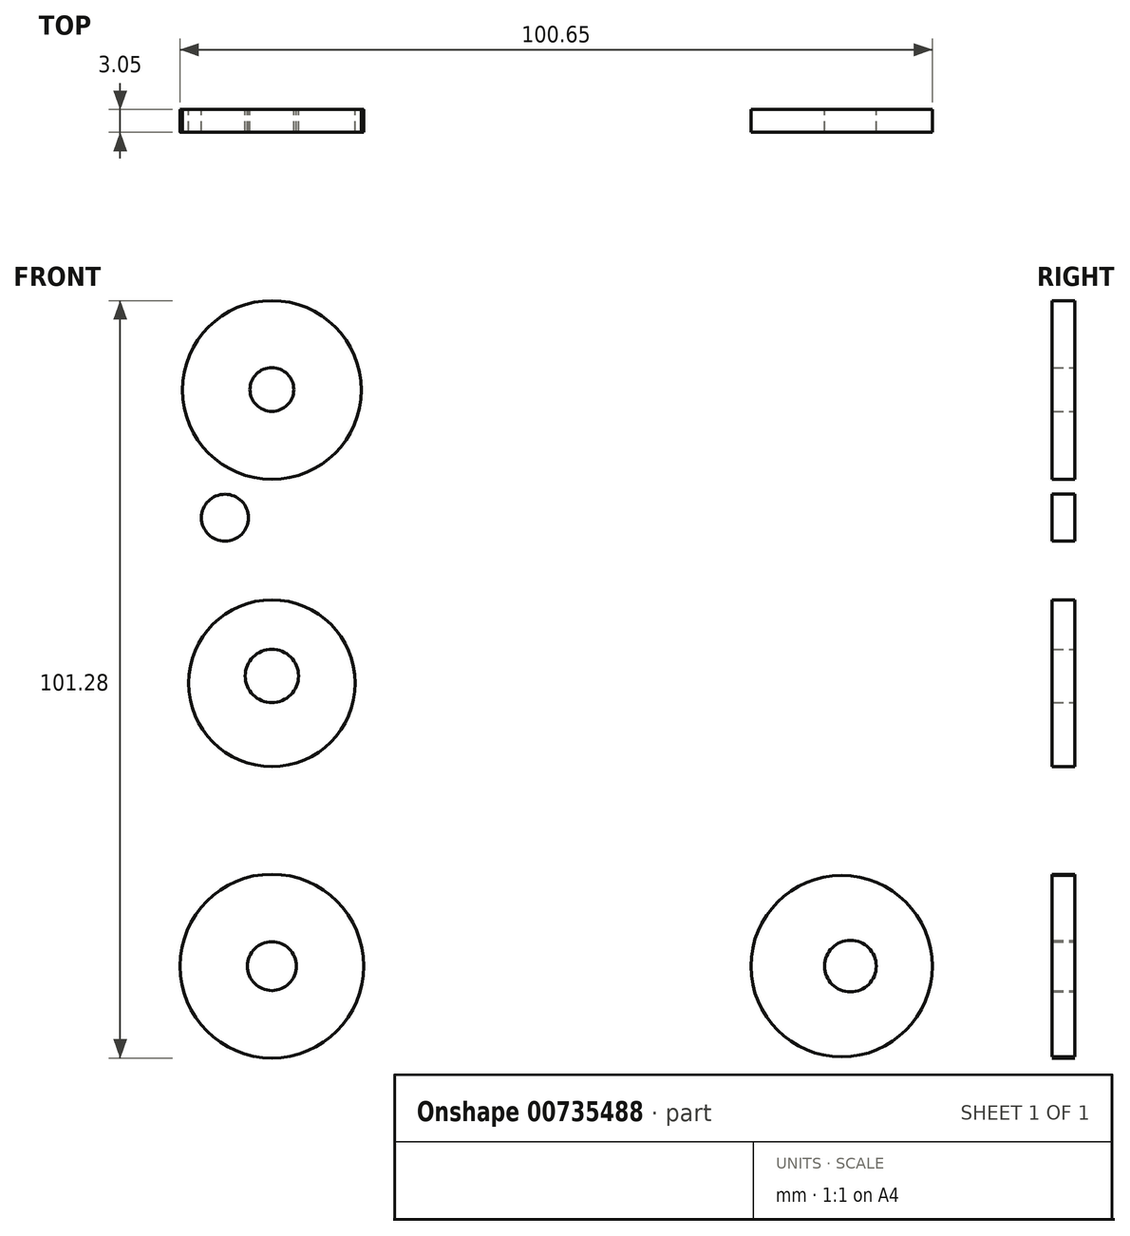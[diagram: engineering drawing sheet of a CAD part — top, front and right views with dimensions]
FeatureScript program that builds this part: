
annotation { "Feature Type Name" : "Feature", "Feature Type Description" : "" }
export const myFeature = defineFeature(function(context is Context, id is Id, definition is map)
    precondition{}
    {
        {
            var Q0;
            Q0=qCreatedBy(makeId("Front.planeOp"),FACE);
            var sketch = newSketch(context, id + "F0", { "sketchPlane" : qUnion([Q0])});
            skCircle(sketch, "E0", {"center": v(0, 0) * mm, "radius": 12.29 * mm});
            skSolve(sketch);
        }
        {
            var Q0;
            Q0=qCreatedBy(makeId("Front.planeOp"),FACE);
            var sketch = newSketch(context, id + "F1", { "sketchPlane" : qUnion([Q0])});
            skCircle(sketch, "E1", {"center": v(0, 37.84) * mm, "radius": 11.14 * mm});
            skSolve(sketch);
        }
        {
            var Q0;
            Q0=qCreatedBy(makeId("Front.planeOp"),FACE);
            var sketch = newSketch(context, id + "F2", { "sketchPlane" : qUnion([Q0])});
            skCircle(sketch, "E2", {"center": v(0, 77.03) * mm, "radius": 11.96 * mm});
            skSolve(sketch);
        }
        {
            var Q0;
            Q0=qCreatedBy(makeId("Front.planeOp"),FACE);
            var sketch = newSketch(context, id + "F3", { "sketchPlane" : qUnion([Q0])});
            skCircle(sketch, "E3", {"center": v(76.23, 0) * mm, "radius": 12.13 * mm});
            skSolve(sketch);
        }
        {
            var Q0;
            Q0=qCreatedBy(makeId("Front.planeOp"),FACE);
            var sketch = newSketch(context, id + "F4", { "sketchPlane" : qUnion([Q0])});
            skLineSegment(sketch, "E4", {"start": v(-11.6, 77.44) * mm, "end": v(-11.6, 37.58) * mm});
            skLineSegment(sketch, "E5", {"start": v(-11.6, 0) * mm, "end": v(-11.6, 37.58) * mm});
            skLineSegment(sketch, "E6", {"start": v(12.29, 77.68) * mm, "end": v(12.29, 37.58) * mm});
            skLineSegment(sketch, "E7", {"start": v(12.29, 0) * mm, "end": v(12.29, 37.58) * mm});
            skLineSegment(sketch, "E8", {"start": v(0, 12.29) * mm, "end": v(76.32, 12.29) * mm});
            skLineSegment(sketch, "E9", {"start": v(0, -13) * mm, "end": v(76.32, -13) * mm});
            skCircle(sketch, "E10", {"center": v(0, 77.1) * mm, "radius": 2.93 * mm});
            skCircle(sketch, "E11", {"center": v(0, 38.8) * mm, "radius": 3.57 * mm});
            skCircle(sketch, "E12", {"center": v(0, 0) * mm, "radius": 3.27 * mm});
            skCircle(sketch, "E13", {"center": v(77.4, 0) * mm, "radius": 3.45 * mm});
            skCircle(sketch, "E14", {"center": v(-6.28, 59.96) * mm, "radius": 3.14 * mm});
            skSolve(sketch);
        }
        {
            var Q0;
            Q0 = qSketchRegion(id + "F0", true);
            extrude(context, id + "F5", {"entities" : qUnion([Q0]), "depth" : 3.05 * mm, "offsetDistance" : 25.4 * mm});
        }
        {
            var Q0;
            Q0 = qSketchRegion(id + "F1", true);
            extrude(context, id + "F6", {"entities" : qUnion([Q0]), "depth" : 3.05 * mm, "offsetDistance" : 25.4 * mm});
        }
        {
            var Q0;
            Q0 = qSketchRegion(id + "F2", true);
            extrude(context, id + "F7", {"entities" : qUnion([Q0]), "depth" : 3.05 * mm, "offsetDistance" : 25.4 * mm});
        }
        {
            var Q0;
            Q0 = qSketchRegion(id + "F3", true);
            extrude(context, id + "F8", {"entities" : qUnion([Q0]), "depth" : 3.05 * mm, "offsetDistance" : 25.4 * mm});
        }
        {
            var Q0;
            Q0 = qSketchRegion(id + "F4", true);
            extrude(context, id + "F9", {"entities" : qUnion([Q0]), "depth" : 3.05 * mm, "offsetDistance" : 25.4 * mm});
        }
    });
